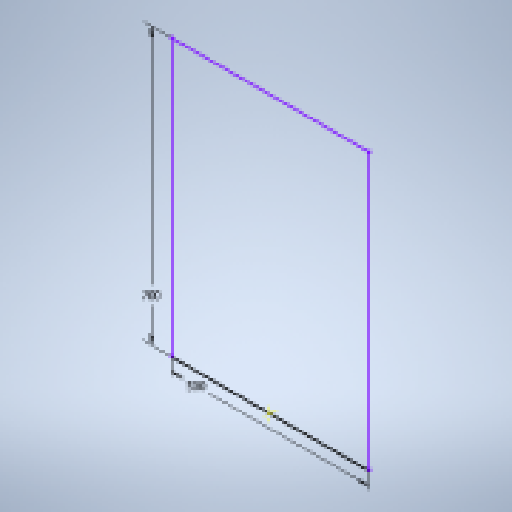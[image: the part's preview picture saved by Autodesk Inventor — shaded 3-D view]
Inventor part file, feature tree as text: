
AUTODESK INVENTOR PART (.ipt)
format: ipt  version: 2024.2 (Build 282272000, 272)  size: 126,464 bytes
history: native  units: in
note: dims shown in document units (in); Inventor stores cm internally (conversion verified against a paired STEP export)
features: sketch x2
ambient origin geometry x8: Origin, YZ Plane, XZ Plane, XY Plane, X Axis, Y Axis, Z Axis, Center Point
feature tree (2):
  sketch  "Sketch3"  dims[d5=19.685in d6=27.5591in]
  sketch  "3D Sketch3"
